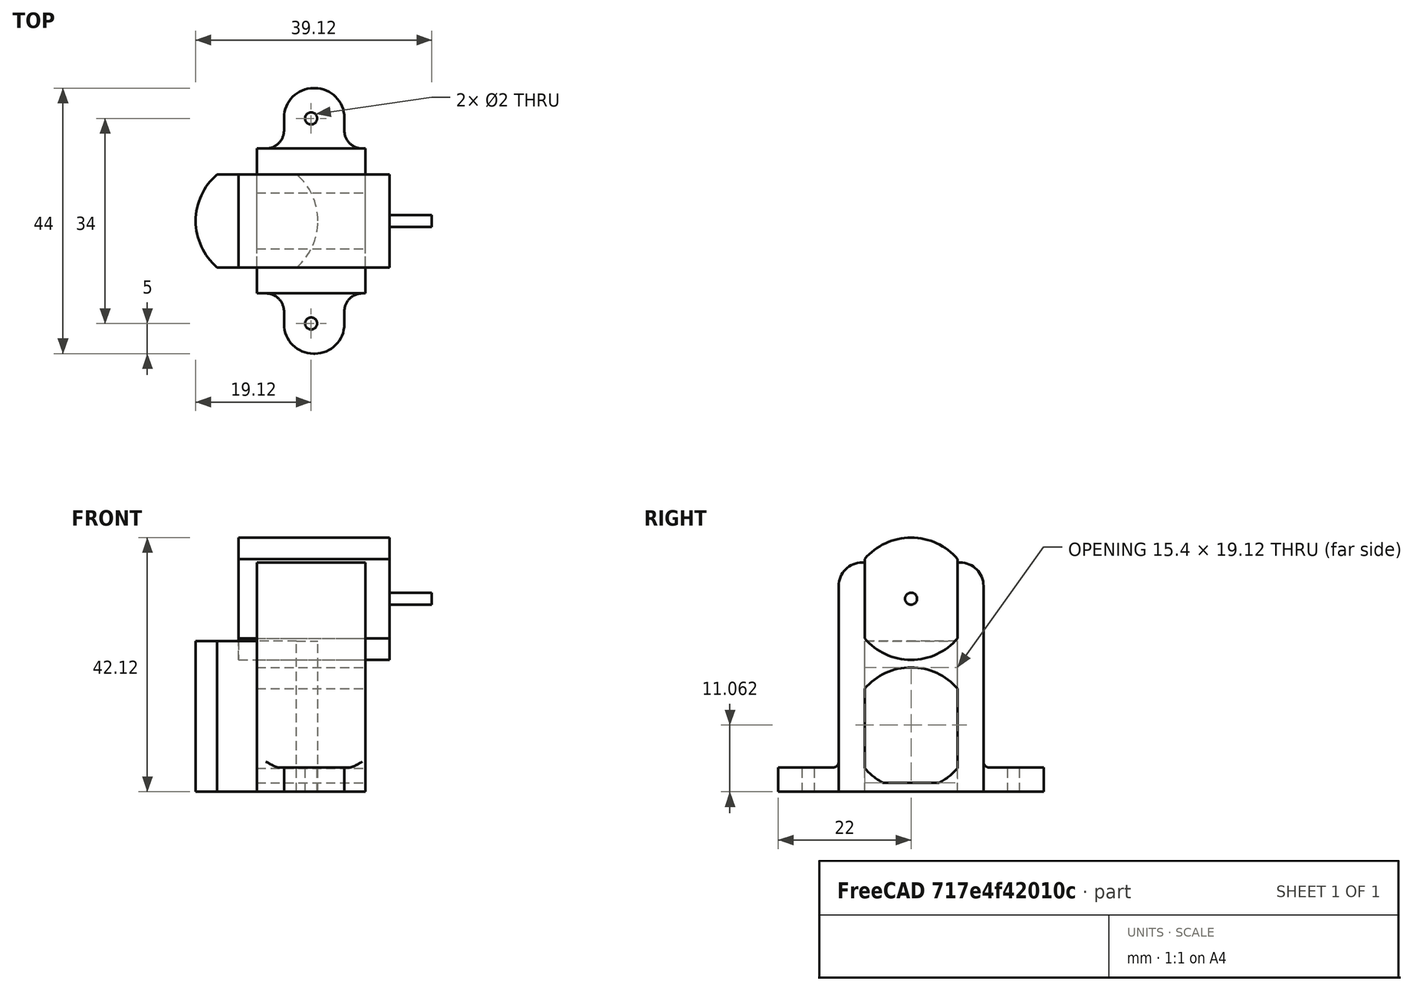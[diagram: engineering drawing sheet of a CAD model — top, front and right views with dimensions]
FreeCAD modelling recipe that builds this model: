
FCSTD DOCUMENT  (FreeCAD 0.17R13541 (Git))
Label: Soporte motor DC D20x15
License: CreativeCommons Attribution
LicenseURL: http://creativecommons.org/licenses/by/4.0/
objects: Part::Cut×5, Part::Box×4, Part::Cylinder×3, Part::MultiFuse×3, Part::Feature×3, Part::Mirroring×2, Part::Fillet×2
note: 22 computed .brp shape members not serialized (recipe doc carries the construction recipe); baked Part::Feature solids carry a one-line shape summary decoded from their .brp

FEATURE [Part::Cylinder] Cylinder  label="Cilindro motor"
  Angle = 360
  AttacherType = Attacher::AttachEngine3D
  Height = 25
  Radius = 10.125
FEATURE [Part::Box] Box  label="Cubo caras planas motor"
  AttacherType = Attacher::AttachEngine3D
  Height = 30
  Length = 25
  Placement = pos=(-12.5,7.7,-3) rot=(0,0,1;0rad)
  Width = 10
FEATURE [Part::Mirroring] Part__Mirroring  label="Cubo caras planas motor (Mirror #1)"
  Base = (0,0,0)
  Normal = (0,1,0)
  Source = -> Box
FEATURE [Part::Box] Box001  label="cuerpo vertical principal"
  AttacherType = Attacher::AttachEngine3D
  Height = 38
  Length = 18
  Placement = pos=(0,-12,0) rot=(0,0,1;0rad)
  Width = 24
FEATURE [Part::Box] Box002  label="master aleta lateral"
  AttacherType = Attacher::AttachEngine3D
  Height = 4
  Length = 10
  Placement = pos=(4.5,12,0) rot=(0,0,1;0rad)
  Width = 10
FEATURE [Part::Cylinder] Cylinder001  label="hueco chincheta"
  Angle = 360
  AttacherType = Attacher::AttachEngine3D
  Height = 10
  Placement = pos=(9,17,-3) rot=(0,0,1;0rad)
  Radius = 1
FEATURE [Part::Fillet] Fillet  label="aleta con radios"
  Base = -> Box002
  Edges = 2 edges r=4.9: [Edge3,Edge7]
FEATURE [Part::Cut] Cut003  label="aleta master"
  Base = -> Fillet
  Refine = true
  Tool = -> Cylinder001
FEATURE [Part::Mirroring] Part__Mirroring001  label="aleta master (Mirror #2)"
  Base = (0,0,0)
  Normal = (0,1,0)
  Source = -> Cut003
FEATURE [Part::MultiFuse] Fusion001  label="Fusion cuerpo con aletas"
  Refine = true
  Shapes = -> [Box001,Cut003,Part__Mirroring001]
FEATURE [Part::MultiFuse] Fusion  label="Fusion prismas caras planas"
  Refine = true
  Shapes = -> [Part__Mirroring,Box]
FEATURE [Part::Cut] Cut  label="Master cuerpo motor con offset 0.2 mm"
  Base = -> Cylinder
  Refine = true
  Tool = -> Fusion
FEATURE [Part::Feature] Cut004  label="Motor con offset"
  Placement = pos=(-3,0,32) rot=(0,1,0;1.5708rad)
  shape: bbox 25 x 15.4 x 20.25 mm, 6 faces (baked)
FEATURE [Part::Cut] Cut005  label="Soporte sin vaciado central001"
  Base = -> Fusion001
  Refine = true
  Tool = -> Cut004
FEATURE [Part::Fillet] Fillet001  label="Soporte sin vaciado central"
  Base = -> Cut005
  Edges = 8 edges: [Edge11 r=3.9,Edge18 r=3.9,Edge21 r=3,Edge22 r=1,Edge23 r=3,Edge41 r=3,Edge42 r=1,Edge43 r=3]
FEATURE [Part::Feature] Cut006  label="copia cuerpo motor"
  shape: bbox 20.25 x 15.4 x 25 mm, 6 faces (baked)
FEATURE [Part::Box] Box003  label="Cubo seccion motor"
  AttacherType = Attacher::AttachEngine3D
  Height = 40
  Length = 11
  Placement = pos=(9,-10,-2) rot=(0,0,1;0rad)
  Width = 20
FEATURE [Part::Cut] Cut007  label="seccion motor"
  Base = -> Cut006
  Placement = pos=(-4,0,10.5) rot=(0,1,0;1.5708rad)
  Refine = true
  Tool = -> Box003
FEATURE [Part::Cut] Cut008  label="Soporte motor DC  D20x15 mm"
  Base = -> Fillet001
  Refine = true
  Tool = -> Cut007
FEATURE [Part::Feature] Cut004001  label="Motor con offset001"
  Placement = pos=(-3,0,32) rot=(0,1,0;1.5708rad)
  shape: bbox 25 x 15.4 x 20.25 mm, 6 faces (baked)
FEATURE [Part::Cylinder] Cylinder002  label="eje motor"
  Angle = 360
  AttacherType = Attacher::AttachEngine3D
  Height = 7
  Placement = pos=(22,0,32) rot=(0,1,0;1.5708rad)
  Radius = 1
FEATURE [Part::MultiFuse] Fusion002  label="Motor"
  Refine = true
  Shapes = -> [Cut004001,Cylinder002]
